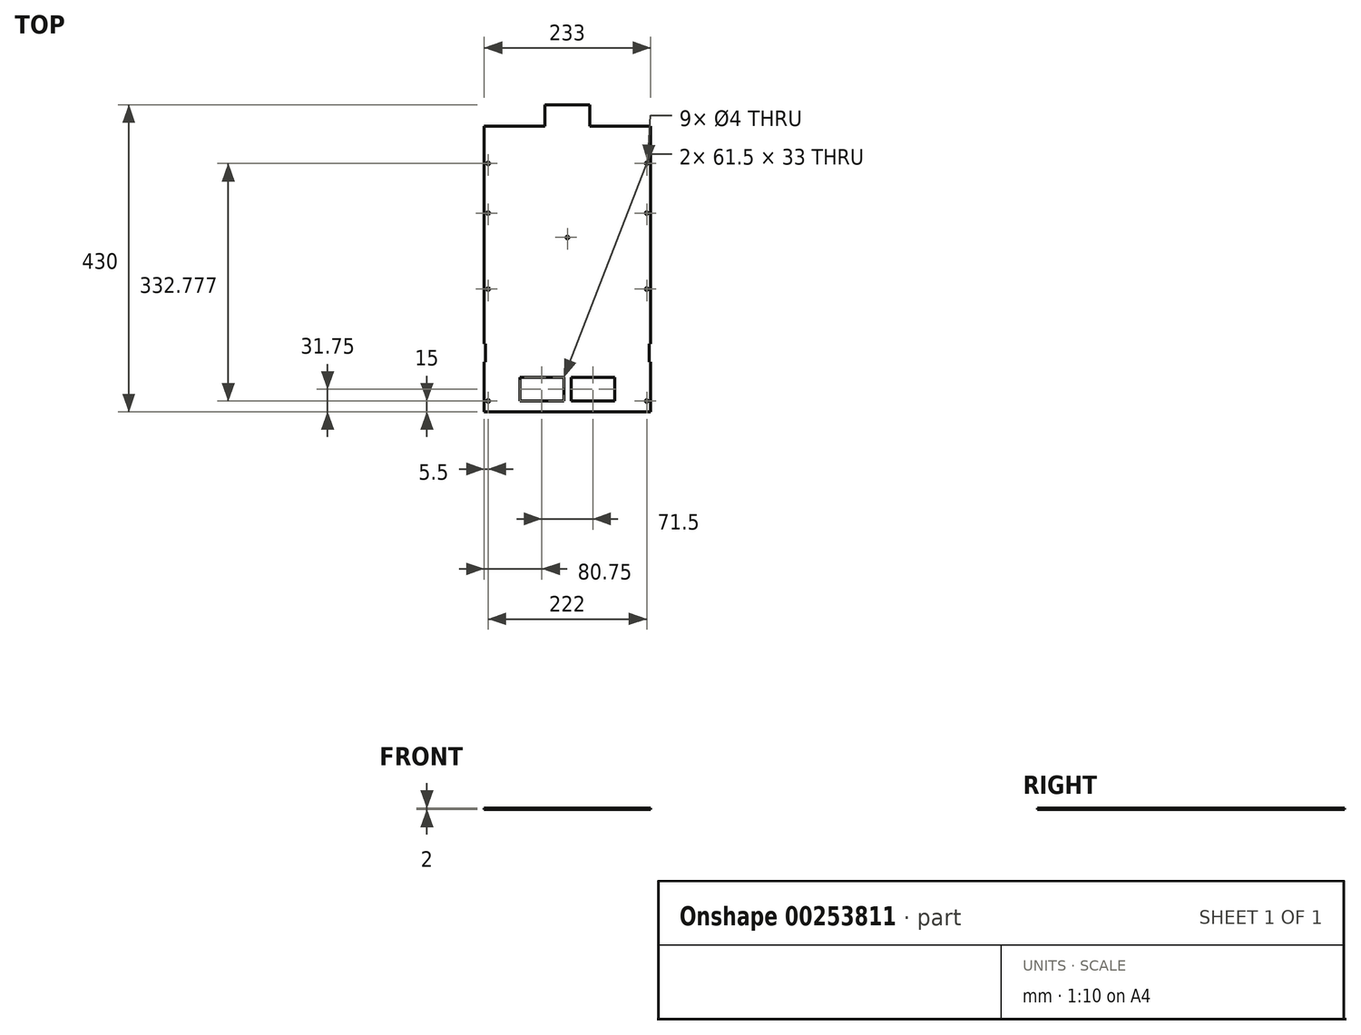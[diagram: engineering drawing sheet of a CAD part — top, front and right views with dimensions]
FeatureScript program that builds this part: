
annotation { "Feature Type Name" : "Feature", "Feature Type Description" : "" }
export const myFeature = defineFeature(function(context is Context, id is Id, definition is map)
    precondition{}
    {
        {
            var Q0;
            Q0=qCreatedBy(makeId("Top.planeOp"),FACE);
            var sketch = newSketch(context, id + "F0", { "sketchPlane" : qUnion([Q0])});
            skLineSegment(sketch, "E0.bottom", {"start": v(116.5, -215) * mm, "end": v(-116.5, -215) * mm});
            skLineSegment(sketch, "E0.top", {"start": v(116.5, 215) * mm, "end": v(-116.5, 215) * mm});
            skLineSegment(sketch, "E0.left", {"start": v(116.5, -215) * mm, "end": v(116.5, 215) * mm});
            skLineSegment(sketch, "E0.right", {"start": v(-116.5, -215) * mm, "end": v(-116.5, 215) * mm});
            skPoint(sketch, "E0.middle", {"position": v(0, 0) * mm});
            skSolve(sketch);
        }
        {
            var Q0;
            Q0 = qSketchRegion(id + "F0", true);
            extrude(context, id + "F1", {"entities" : qUnion([Q0]), "depth" : 2 * mm});
        }
        {
            var Q0;
            Q0=makeQuery(id+"F1.opExtrude","CAP_FACE",FACE,{"disambiguationData":[OSD([sQuery(id+"F0.wireOp",EDGE,"E0.bottom"),sQuery(id+"F0.wireOp",EDGE,"E0.top"),sQuery(id+"F0.wireOp",EDGE,"E0.left"),sQuery(id+"F0.wireOp",EDGE,"E0.right")])],"isStart":false});
            var sketch = newSketch(context, id + "F2", { "sketchPlane" : qUnion([Q0])});
            skLineSegment(sketch, "E1.bottom", {"start": v(-116.5, 215) * mm, "end": v(-31.5, 215) * mm});
            skLineSegment(sketch, "E1.top", {"start": v(-116.5, 185) * mm, "end": v(-31.5, 185) * mm});
            skLineSegment(sketch, "E1.left", {"start": v(-116.5, 215) * mm, "end": v(-116.5, 185) * mm});
            skLineSegment(sketch, "E1.right", {"start": v(-31.5, 215) * mm, "end": v(-31.5, 185) * mm});
            skLineSegment(sketch, "E2.bottom", {"start": v(116.5, 215) * mm, "end": v(31.5, 215) * mm});
            skLineSegment(sketch, "E2.top", {"start": v(116.5, 185) * mm, "end": v(31.5, 185) * mm});
            skLineSegment(sketch, "E2.left", {"start": v(116.5, 215) * mm, "end": v(116.5, 185) * mm});
            skLineSegment(sketch, "E2.right", {"start": v(31.5, 215) * mm, "end": v(31.5, 185) * mm});
            skLineSegment(sketch, "E3.bottom", {"start": v(-66.5, -166.75) * mm, "end": v(-5, -166.75) * mm});
            skLineSegment(sketch, "E3.top", {"start": v(-66.5, -199.75) * mm, "end": v(-5, -199.75) * mm});
            skLineSegment(sketch, "E3.left", {"start": v(-66.5, -166.75) * mm, "end": v(-66.5, -199.75) * mm});
            skLineSegment(sketch, "E3.right", {"start": v(-5, -166.75) * mm, "end": v(-5, -199.75) * mm});
            skLineSegment(sketch, "E4.bottom", {"start": v(5, -166.75) * mm, "end": v(66.5, -166.75) * mm});
            skLineSegment(sketch, "E4.top", {"start": v(5, -199.75) * mm, "end": v(66.5, -199.75) * mm});
            skLineSegment(sketch, "E4.left", {"start": v(5, -166.75) * mm, "end": v(5, -199.75) * mm});
            skLineSegment(sketch, "E4.right", {"start": v(66.5, -166.75) * mm, "end": v(66.5, -199.75) * mm});
            skLineSegment(sketch, "E5.bottom", {"start": v(-116.5, -120) * mm, "end": v(-114.5, -120) * mm});
            skLineSegment(sketch, "E5.top", {"start": v(-116.5, -145) * mm, "end": v(-114.5, -145) * mm});
            skLineSegment(sketch, "E5.left", {"start": v(-116.5, -120) * mm, "end": v(-116.5, -145) * mm});
            skLineSegment(sketch, "E5.right", {"start": v(-114.5, -120) * mm, "end": v(-114.5, -145) * mm});
            skLineSegment(sketch, "E6.bottom", {"start": v(116.5, -120) * mm, "end": v(114.5, -120) * mm});
            skLineSegment(sketch, "E6.top", {"start": v(116.5, -145) * mm, "end": v(114.5, -145) * mm});
            skLineSegment(sketch, "E6.left", {"start": v(116.5, -120) * mm, "end": v(116.5, -145) * mm});
            skLineSegment(sketch, "E6.right", {"start": v(114.5, -120) * mm, "end": v(114.5, -145) * mm});
            skCircle(sketch, "E7", {"center": v(-111, 132.78) * mm, "radius": 2 * mm});
            skCircle(sketch, "E8", {"center": v(111, 132.78) * mm, "radius": 2 * mm});
            skCircle(sketch, "E9", {"center": v(-111, 63.29) * mm, "radius": 2 * mm});
            skCircle(sketch, "E10", {"center": v(111, 63.29) * mm, "radius": 2 * mm});
            skCircle(sketch, "E11", {"center": v(-111, -43.2) * mm, "radius": 2 * mm});
            skCircle(sketch, "E12", {"center": v(111, -43.2) * mm, "radius": 2 * mm});
            skCircle(sketch, "E13", {"center": v(111, -200) * mm, "radius": 2 * mm});
            skCircle(sketch, "E14", {"center": v(-111, -200) * mm, "radius": 2 * mm});
            skCircle(sketch, "E15", {"center": v(0, 29.13) * mm, "radius": 2 * mm});
            skSolve(sketch);
        }
        {
            var Q0;
            Q0 = qSketchRegion(id + "F2", true);
            extrude(context, id + "F3", {"entities" : qUnion([Q0]), "operationType" : NewBodyOperationType.REMOVE, "endBound" : BoundingType.THROUGH_ALL, "oppositeDirection" : true, "depth" : 25 * mm});
        }
    });
